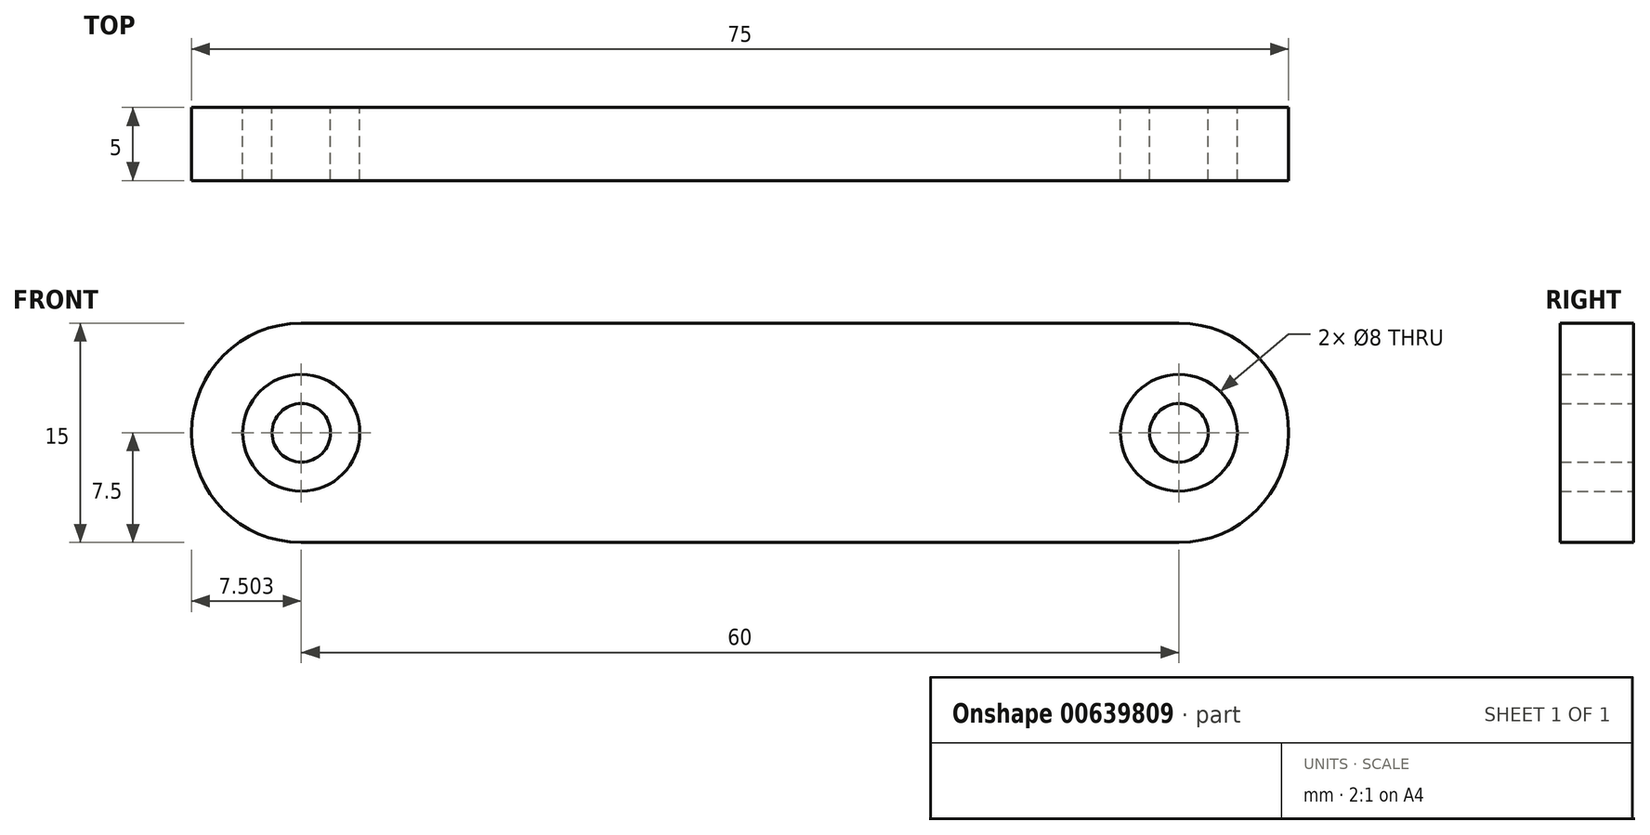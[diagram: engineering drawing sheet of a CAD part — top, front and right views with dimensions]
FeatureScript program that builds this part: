
annotation { "Feature Type Name" : "Feature", "Feature Type Description" : "" }
export const myFeature = defineFeature(function(context is Context, id is Id, definition is map)
    precondition{}
    {
        {
            var Q0;
            Q0=qCreatedBy(makeId("Front.planeOp"),FACE);
            var sketch = newSketch(context, id + "F0", { "sketchPlane" : qUnion([Q0])});
            skArc(sketch, "E0", {"start": v(-32.55, 7.5) * mm, "mid": v(-40.05, 0) * mm, "end": v(-32.55, -7.5) * mm});
            skArc(sketch, "E1", {"start": v(27.45, -7.5) * mm, "mid": v(34.95, 0) * mm, "end": v(27.45, 7.5) * mm});
            skCircle(sketch, "E2", {"center": v(-32.55, 0) * mm, "radius": 4 * mm});
            skCircle(sketch, "E3", {"center": v(27.45, 0) * mm, "radius": 4 * mm});
            skCircle(sketch, "E4", {"center": v(27.45, 0) * mm, "radius": 2 * mm});
            skCircle(sketch, "E5", {"center": v(-32.55, 0) * mm, "radius": 2 * mm});
            skLineSegment(sketch, "E6", {"start": v(-32.55, 7.5) * mm, "end": v(27.45, 7.5) * mm});
            skLineSegment(sketch, "E7", {"start": v(-32.55, -7.5) * mm, "end": v(27.45, -7.5) * mm});
            skSolve(sketch);
        }
        {
            var Q0;
            Q0=makeQuery(id+"F0.imprint","IMPRINT",FACE,{"disambiguationData":[TD([[makeQuery(id+"F0.imprint","IMPRINT",EDGE,{"derivedFrom":sQuery(id+"F0.wireOp",EDGE,"E0")}),1.0]])]});
            var Q1;
            Q1=makeQuery(id+"F0.imprint","IMPRINT",FACE,{"disambiguationData":[TD([[makeQuery(id+"F0.imprint","IMPRINT",EDGE,{"derivedFrom":sQuery(id+"F0.wireOp",EDGE,"E5")}),1.0]])]});
            var Q2;
            Q2=makeQuery(id+"F0.imprint","IMPRINT",FACE,{"disambiguationData":[TD([[makeQuery(id+"F0.imprint","IMPRINT",EDGE,{"derivedFrom":sQuery(id+"F0.wireOp",EDGE,"E4")}),1.0]])]});
            extrude(context, id + "F1", {"entities" : qUnion([Q0, Q1, Q2]), "depth" : 5 * mm, "offsetDistance" : 25.4 * mm});
        }
    });
